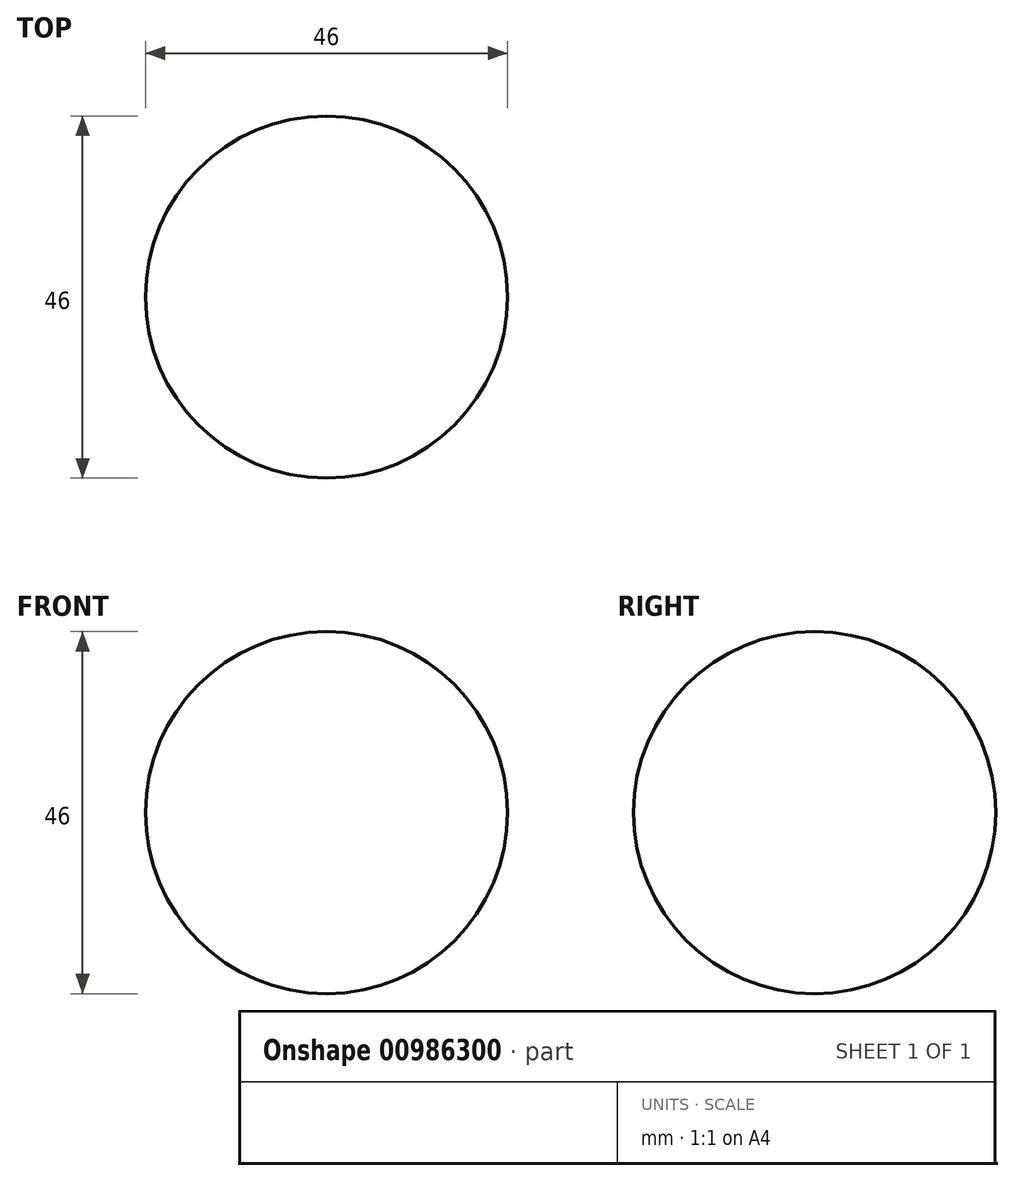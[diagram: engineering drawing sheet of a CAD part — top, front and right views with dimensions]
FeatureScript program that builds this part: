
annotation { "Feature Type Name" : "Feature", "Feature Type Description" : "" }
export const myFeature = defineFeature(function(context is Context, id is Id, definition is map)
    precondition{}
    {
        {
            var Q0;
            Q0=qCreatedBy(makeId("Front.planeOp"),FACE);
            var sketch = newSketch(context, id + "F0", { "sketchPlane" : qUnion([Q0])});
            skArc(sketch, "E0", {"start": v(0, -23) * mm, "mid": v(23, 0) * mm, "end": v(0, 23) * mm});
            skLineSegment(sketch, "E1", {"start": v(0, 23) * mm, "end": v(0, -23) * mm});
            skSolve(sketch);
        }
        {
            var Q0;
            Q0 = qSketchRegion(id + "F0", true);
            var Q1;
            Q1=sQuery(id+"F0.wireOp",EDGE,"E1");
            revolve(context, id + "F1", {"surfaceOperationType" : NewSurfaceOperationType.NEW, "entities" : qUnion([Q0]), "axis" : qUnion([Q1]), "revolveType" : RevolveType.FULL});
        }
    });
